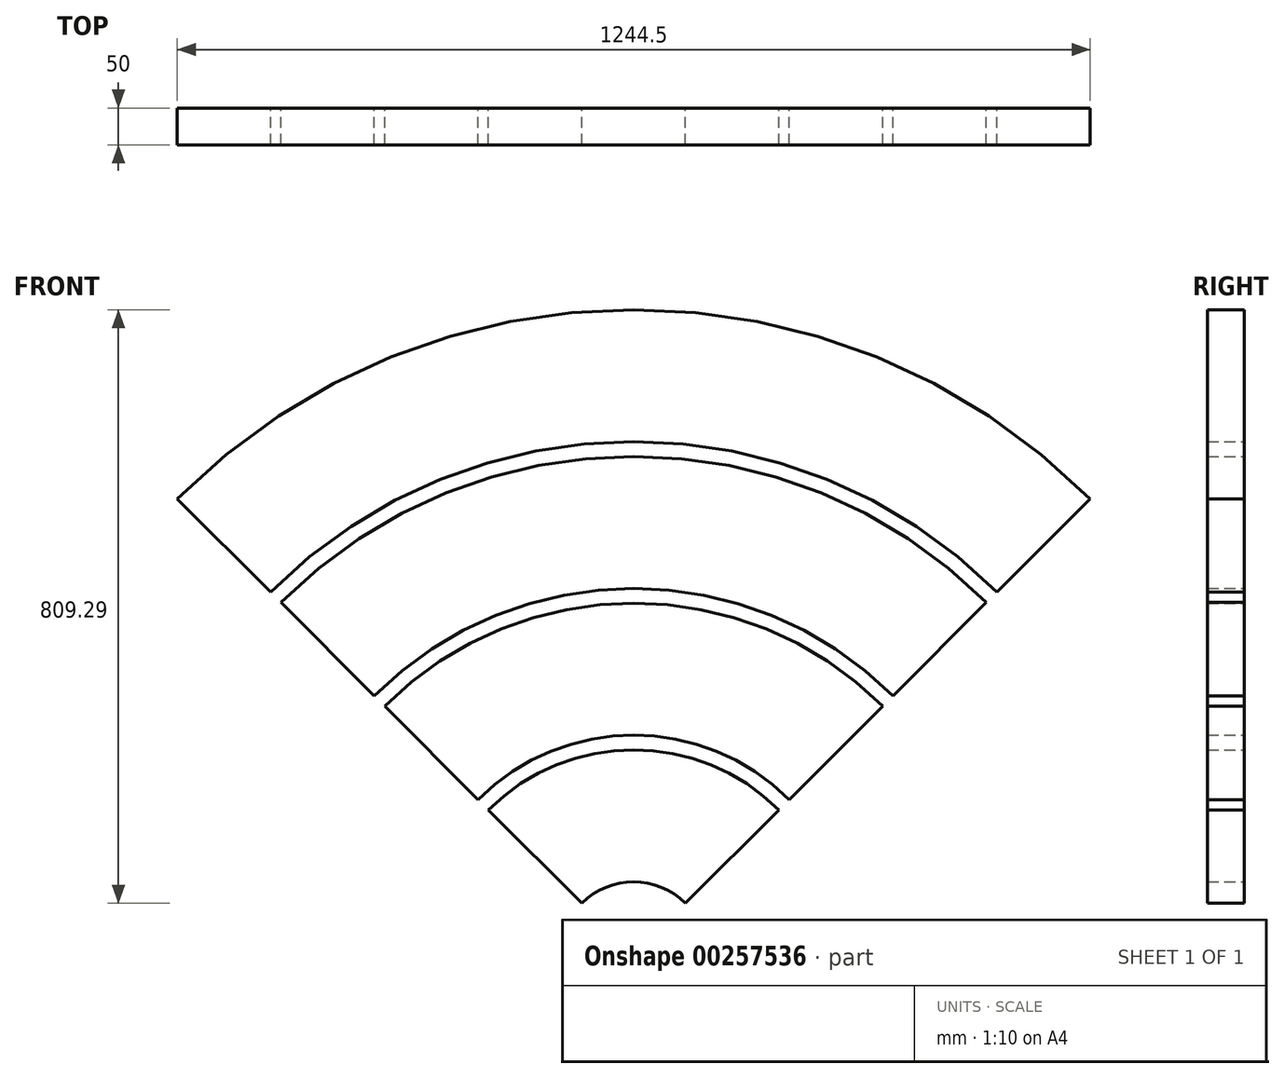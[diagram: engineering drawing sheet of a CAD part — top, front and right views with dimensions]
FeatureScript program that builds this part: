
annotation { "Feature Type Name" : "Feature", "Feature Type Description" : "" }
export const myFeature = defineFeature(function(context is Context, id is Id, definition is map)
    precondition{}
    {
        {
            var Q0;
            Q0=qCreatedBy(makeId("Front.planeOp"),FACE);
            var sketch = newSketch(context, id + "F0", { "sketchPlane" : qUnion([Q0])});
            skLineSegment(sketch, "E0", {"start": v(0, 0) * mm, "end": v(-707.1, 707.1) * mm});
            skLineSegment(sketch, "E1", {"start": v(0, 0) * mm, "end": v(707.1, 707.1) * mm});
            skArc(sketch, "E2", {"start": v(-353.55, 353.55) * mm, "mid": v(0, 500) * mm, "end": v(353.55, 353.55) * mm});
            skArc(sketch, "E3", {"start": v(-636.4, 636.4) * mm, "mid": v(0, 900) * mm, "end": v(636.4, 636.4) * mm});
            skArc(sketch, "E4", {"start": v(-212.13, 212.13) * mm, "mid": v(0, 300) * mm, "end": v(212.13, 212.13) * mm});
            skArc(sketch, "E5", {"start": v(-494.97, 494.97) * mm, "mid": v(0, 700) * mm, "end": v(494.97, 494.97) * mm});
            skArc(sketch, "E6.0", {"start": v(-622.25, 622.25) * mm, "mid": v(0, 880) * mm, "end": v(622.25, 622.25) * mm});
            skArc(sketch, "E7.0", {"start": v(-480.83, 480.83) * mm, "mid": v(0, 680) * mm, "end": v(480.83, 480.83) * mm});
            skArc(sketch, "E8.0", {"start": v(-339.41, 339.41) * mm, "mid": v(0, 480) * mm, "end": v(339.41, 339.41) * mm});
            skArc(sketch, "E9.0", {"start": v(-197.99, 197.99) * mm, "mid": v(0, 280) * mm, "end": v(197.99, 197.99) * mm});
            skArc(sketch, "E10", {"start": v(-70.71, 70.71) * mm, "mid": v(0, 100) * mm, "end": v(70.71, 70.71) * mm});
            skArc(sketch, "E11.0", {"start": v(-56.57, 56.57) * mm, "mid": v(0, 80) * mm, "end": v(56.57, 56.57) * mm});
            skSolve(sketch);
        }
        {
            var Q0;
            {var subQ0=sQuery(id+"F0.wireOp",EDGE,"E3");Q0=makeQuery(id+"F0.imprint","IMPRINT",FACE,{"disambiguationData":[TD([[makeQuery(id+"F0.imprint","IMPRINT",EDGE,{"derivedFrom":subQ0}),-1.0]])]});}
            var Q1;
            {var subQ0=sQuery(id+"F0.wireOp",EDGE,"E5");Q1=makeQuery(id+"F0.imprint","IMPRINT",FACE,{"disambiguationData":[TD([[makeQuery(id+"F0.imprint","IMPRINT",EDGE,{"derivedFrom":subQ0}),-1.0]])]});}
            var Q2;
            {var subQ0=sQuery(id+"F0.wireOp",EDGE,"E2");Q2=makeQuery(id+"F0.imprint","IMPRINT",FACE,{"disambiguationData":[TD([[makeQuery(id+"F0.imprint","IMPRINT",EDGE,{"derivedFrom":subQ0}),-1.0]])]});}
            var Q3;
            {var subQ0=sQuery(id+"F0.wireOp",EDGE,"E4");Q3=makeQuery(id+"F0.imprint","IMPRINT",FACE,{"disambiguationData":[TD([[makeQuery(id+"F0.imprint","IMPRINT",EDGE,{"derivedFrom":subQ0}),-1.0]])]});}
            var Q4;
            {var subQ0=sQuery(id+"F0.wireOp",EDGE,"E10");Q4=makeQuery(id+"F0.imprint","IMPRINT",FACE,{"disambiguationData":[TD([[makeQuery(id+"F0.imprint","IMPRINT",EDGE,{"derivedFrom":subQ0}),-1.0]])]});}
            extrude(context, id + "F1", {"entities" : qUnion([Q0, Q1, Q2, Q3, Q4]), "depth" : 25 * mm, "hasSecondDirection" : true, "secondDirectionOppositeDirection" : true, "secondDirectionDepth" : 25 * mm});
        }
    });
